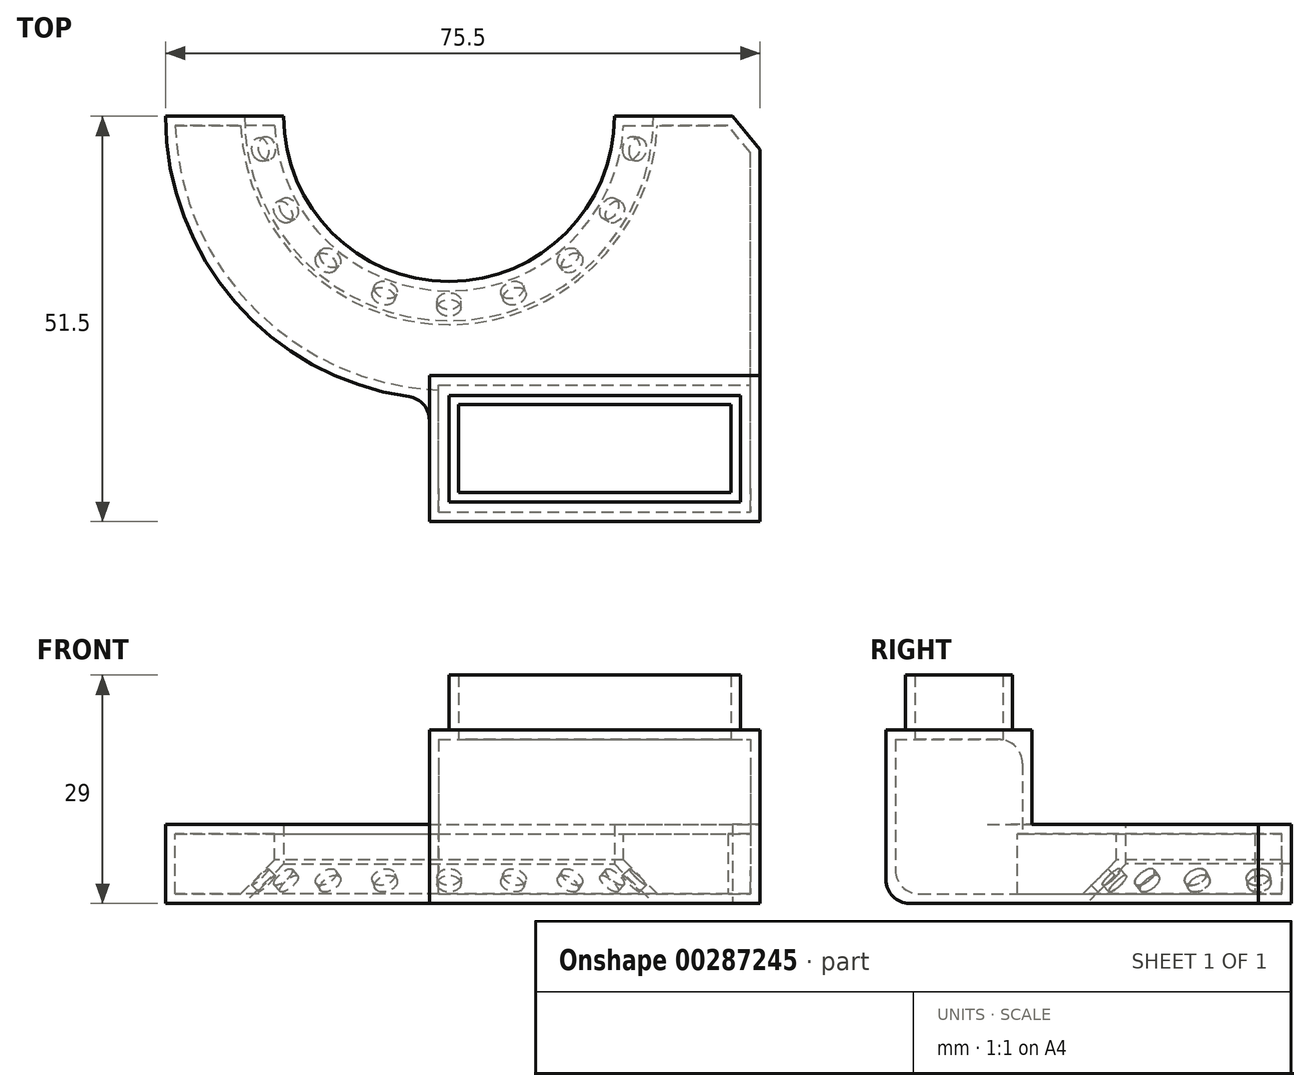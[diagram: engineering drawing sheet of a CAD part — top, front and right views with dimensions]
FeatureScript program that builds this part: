
annotation { "Feature Type Name" : "Feature", "Feature Type Description" : "" }
export const myFeature = defineFeature(function(context is Context, id is Id, definition is map)
    precondition{}
    {
        {
            var Q0;
            Q0=qCreatedBy(makeId("Front.planeOp"),FACE);
            var sketch = newSketch(context, id + "F0", { "sketchPlane" : qUnion([Q0])});
            skLineSegment(sketch, "E0", {"start": v(0, 66.2) * mm, "end": v(0, -56.66) * mm, "construction": true});
            skLineSegment(sketch, "E1", {"start": v(21, 10) * mm, "end": v(36, 10) * mm});
            skLineSegment(sketch, "E2", {"start": v(36, 10) * mm, "end": v(36, 0) * mm});
            skLineSegment(sketch, "E3", {"start": v(36, 0) * mm, "end": v(26, 0) * mm});
            skLineSegment(sketch, "E4", {"start": v(21, 10) * mm, "end": v(21, 5) * mm});
            skLineSegment(sketch, "E5", {"start": v(21, 5) * mm, "end": v(26, 0) * mm});
            skSolve(sketch);
        }
        {
            var Q0;
            Q0=makeQuery(id+"F0.imprint","IMPRINT",FACE,{"disambiguationData":[TD([[makeQuery(id+"F0.imprint","IMPRINT",EDGE,{"derivedFrom":sQuery(id+"F0.wireOp",EDGE,"E1")}),-1.0]])]});
            var Q1;
            Q1=sQuery(id+"F0.wireOp",EDGE,"E0");
            revolve(context, id + "F1", {"entities" : qUnion([Q0]), "axis" : qUnion([Q1]), "revolveType" : RevolveType.TWO_DIRECTIONS, "angle" : 180 * degree, "angleBack" : 360 * degree});
        }
        {
            var Q0;
            Q0=qCreatedBy(makeId("Top.planeOp"),FACE);
            var sketch = newSketch(context, id + "F2", { "sketchPlane" : qUnion([Q0])});
            skLineSegment(sketch, "E6.bottom", {"start": v(-2.5, -51.5) * mm, "end": v(39.5, -51.5) * mm});
            skLineSegment(sketch, "E6.left", {"start": v(-2.5, -51.5) * mm, "end": v(-2.5, -30.9) * mm});
            skLineSegment(sketch, "E6.right", {"start": v(39.5, -51.5) * mm, "end": v(39.5, -4.22) * mm});
            skPoint(sketch, "E7.orphan", {"position": v(26, 0) * mm});
            skPoint(sketch, "E8.orphan", {"position": v(-26, 0) * mm});
            skPoint(sketch, "E9.0", {"position": v(36, 0) * mm});
            skLineSegment(sketch, "E10", {"start": v(39.5, -4.22) * mm, "end": v(36, 0) * mm});
            skArc(sketch, "E11", {"start": v(-2.5, -30.9) * mm, "mid": v(21.02, -22.79) * mm, "end": v(31, 0) * mm});
            skLineSegment(sketch, "E12", {"start": v(36, 0) * mm, "end": v(31, 0) * mm});
            skSolve(sketch);
        }
        {
            var Q0;
            Q0=makeQuery(id+"F2.imprint","IMPRINT",FACE,{"disambiguationData":[TD([[makeQuery(id+"F2.imprint","IMPRINT",EDGE,{"derivedFrom":sQuery(id+"F2.wireOp",EDGE,"E6.bottom")}),1.0]])]});
            var Q1;
            Q1=makeQuery(id+"F1.opRevolve","SWEPT_FACE",FACE,{"disambiguationData":[OSD([sQuery(id+"F0.wireOp",EDGE,"E1")])]});
            extrude(context, id + "F3", {"entities" : qUnion([Q0]), "operationType" : NewBodyOperationType.ADD, "endBound" : BoundingType.UP_TO_SURFACE, "endBoundEntityFace" : qUnion([Q1]), "depth" : 25 * mm});
        }
        {
            var Q0;
            Q0=makeQuery(id+"F3.boolean.opBoolean","MERGE",FACE,{"derivedFrom":[makeQuery(id+"F1.opRevolve","SWEPT_FACE",FACE,{"disambiguationData":[OSD([sQuery(id+"F0.wireOp",EDGE,"E1")])]}),makeQuery(id+"F3.opExtrude","CAP_FACE",FACE,{"disambiguationData":[OSD([sQuery(id+"F2.wireOp",EDGE,"E6.bottom"),sQuery(id+"F2.wireOp",EDGE,"E6.left"),sQuery(id+"F2.wireOp",EDGE,"E6.right"),sQuery(id+"F2.wireOp",EDGE,"E10"),sQuery(id+"F2.wireOp",EDGE,"E11"),sQuery(id+"F2.wireOp",EDGE,"E12")])],"isStart":false})]});
            var sketch = newSketch(context, id + "F4", { "sketchPlane" : qUnion([Q0])});
            skPoint(sketch, "E13.0", {"position": v(-2.5, -51.5) * mm});
            skLineSegment(sketch, "E14.bottom", {"start": v(-2.5, -51.5) * mm, "end": v(39.5, -51.5) * mm});
            skLineSegment(sketch, "E14.top", {"start": v(-2.5, -32.96) * mm, "end": v(39.5, -32.96) * mm});
            skLineSegment(sketch, "E14.left", {"start": v(-2.5, -51.5) * mm, "end": v(-2.5, -32.96) * mm});
            skLineSegment(sketch, "E14.right", {"start": v(39.5, -51.5) * mm, "end": v(39.5, -32.96) * mm});
            skSolve(sketch);
        }
        {
            var Q0;
            Q0=makeQuery(id+"F4.imprint","IMPRINT",FACE,{"disambiguationData":[TD([[makeQuery(id+"F4.imprint","IMPRINT",EDGE,{"derivedFrom":sQuery(id+"F4.wireOp",EDGE,"E14.bottom")}),1.0]])]});
            extrude(context, id + "F5", {"entities" : qUnion([Q0]), "operationType" : NewBodyOperationType.ADD, "depth" : 12 * mm});
        }
        {
            var Q0;
            Q0=makeQuery(id+"F5.opExtrude","CAP_FACE",FACE,{"disambiguationData":[OSD([sQuery(id+"F4.wireOp",EDGE,"E14.bottom"),sQuery(id+"F4.wireOp",EDGE,"E14.top"),sQuery(id+"F4.wireOp",EDGE,"E14.left"),sQuery(id+"F4.wireOp",EDGE,"E14.right")])],"isStart":false});
            var sketch = newSketch(context, id + "F6", { "sketchPlane" : qUnion([Q0])});
            skPoint(sketch, "E15.0", {"position": v(-2.5, -32.96) * mm});
            skPoint(sketch, "E16.0", {"position": v(-2.5, -51.5) * mm});
            skPoint(sketch, "E17.0", {"position": v(39.5, -51.5) * mm});
            skPoint(sketch, "E18.0", {"position": v(39.5, -32.96) * mm});
            skLineSegment(sketch, "E19", {"start": v(-2.5, -32.96) * mm, "end": v(39.5, -51.5) * mm, "construction": true});
            skLineSegment(sketch, "E20", {"start": v(-2.5, -51.5) * mm, "end": v(39.5, -32.96) * mm, "construction": true});
            skLineSegment(sketch, "E21.bottom", {"start": v(37, -35.46) * mm, "end": v(0, -35.46) * mm});
            skLineSegment(sketch, "E21.top", {"start": v(37, -49) * mm, "end": v(0, -49) * mm});
            skLineSegment(sketch, "E21.left", {"start": v(37, -35.46) * mm, "end": v(37, -49) * mm});
            skLineSegment(sketch, "E21.right", {"start": v(0, -35.46) * mm, "end": v(0, -49) * mm});
            skPoint(sketch, "E21.middle", {"position": v(18.5, -42.23) * mm});
            skSolve(sketch);
        }
        {
            var Q0;
            Q0=makeQuery(id+"F6.imprint","IMPRINT",FACE,{"disambiguationData":[TD([[makeQuery(id+"F6.imprint","IMPRINT",EDGE,{"derivedFrom":sQuery(id+"F6.wireOp",EDGE,"E21.bottom")}),1.0]])]});
            extrude(context, id + "F7", {"entities" : qUnion([Q0]), "operationType" : NewBodyOperationType.ADD, "depth" : 7 * mm});
        }
        {
            var Q0;
            Q0=makeQuery(id+"F7.opExtrude","CAP_FACE",FACE,{"disambiguationData":[OSD([sQuery(id+"F6.wireOp",EDGE,"E21.bottom"),sQuery(id+"F6.wireOp",EDGE,"E21.top"),sQuery(id+"F6.wireOp",EDGE,"E21.left"),sQuery(id+"F6.wireOp",EDGE,"E21.right")])],"isStart":false});
            shell(context, id + "F8", {"entities" : qUnion([Q0]), "thickness" : 1.2 * mm});
        }
        {
            var Q0;
            Q0=qCreatedBy(makeId("Top.planeOp"),FACE);
            var sketch = newSketch(context, id + "F9", { "sketchPlane" : qUnion([Q0])});
            skLineSegment(sketch, "E22", {"start": v(71.7, 0) * mm, "end": v(-68.59, 0) * mm});
            skSolve(sketch);
        }
        {
            var Q0;
            Q0=sQuery(id+"F9.wireOp",EDGE,"E22");
            cPlane(context, id + "F10", {"entities" : qUnion([Q0]), "cplaneType" : CPlaneType.LINE_ANGLE, "offset" : 25 * mm, "angle" : 45 * degree, "width" : 150 * mm, "height" : 150 * mm});
        }
        {
            var Q0;
            Q0=qCreatedBy(id+"F10.planeOp",FACE);
            var sketch = newSketch(context, id + "F11", { "sketchPlane" : qUnion([Q0])});
            skCircle(sketch, "E23", {"center": v(0, -14.85) * mm, "radius": 1.5 * mm});
            skSolve(sketch);
        }
        {
            var Q0;
            Q0=makeQuery(id+"F11.imprint","IMPRINT",FACE,{"disambiguationData":[TD([[makeQuery(id+"F11.imprint","IMPRINT",EDGE,{"derivedFrom":sQuery(id+"F11.wireOp",EDGE,"E23")}),1.0]])]});
            extrude(context, id + "F12", {"entities" : qUnion([Q0]), "depth" : 25 * mm});
        }
        {
            var Q0;
            Q0=makeQuery(id+"F12.opExtrude","SWEPT_BODY",BODY,{"disambiguationData":[OSD([sQuery(id+"F11.wireOp",EDGE,"E23")])]});
            var Q1;
            Q1=sQuery(id+"F0.wireOp",EDGE,"E0");
            circularPattern(context, id + "F13", {"operationType" : NewBodyOperationType.REMOVE, "entities" : qUnion([Q0]), "axis" : qUnion([Q1]), "angle" : 360 * degree, "instanceCount" : 18, "equalSpace" : true});
        }
        {
            var Q0;
            Q0=makeQuery(id+"F3.opExtrude","CAP_EDGE",EDGE,{"disambiguationData":[OSD([sQuery(id+"F2.wireOp",EDGE,"E6.bottom")])],"isStart":true});
            var Q1;
            Q1=makeQuery(id+"F8.opShell","OFFSET_EDGE",EDGE,{"disambiguationData":[OSD([sQuery(id+"F2.wireOp",EDGE,"E6.bottom")])]});
            var Q2;
            {var subQ0=sQuery(id+"F4.wireOp",EDGE,"E14.top");Q2=makeQuery(id+"F8.opShell","OFFSET_EDGE",EDGE,{"disambiguationData":[OSD([subQ0]),TDD([makeQuery(id+"F5.opExtrude","CAP_EDGE",EDGE,{"disambiguationData":[OSD([subQ0])],"isStart":true})])]});}
            var Q3;
            Q3=makeQuery(id+"F5.opExtrude","CAP_EDGE",EDGE,{"disambiguationData":[OSD([sQuery(id+"F4.wireOp",EDGE,"E14.top")])],"isStart":true});
            var Q4;
            Q4=makeQuery(id+"F3.boolean.opBoolean","INTERSECT",EDGE,{"derivedFrom":[makeQuery(id+"F1.opRevolve","SWEPT_FACE",FACE,{"disambiguationData":[OSD([sQuery(id+"F0.wireOp",EDGE,"E2")])]}),makeQuery(id+"F3.opExtrude","SWEPT_FACE",FACE,{"disambiguationData":[OSD([sQuery(id+"F2.wireOp",EDGE,"E6.left")])]})]});
            var Q5;
            Q5=makeQuery(id+"F3.boolean.opBoolean","INTERSECT",EDGE,{"derivedFrom":[makeQuery(id+"F1.opRevolve","SWEPT_FACE",FACE,{"disambiguationData":[OSD([sQuery(id+"F0.wireOp",EDGE,"E2")])]}),makeQuery(id+"F3.opExtrude","SWEPT_FACE",FACE,{"disambiguationData":[OSD([sQuery(id+"F2.wireOp",EDGE,"E6.left")])]})]});
            fillet(context, id + "F14", {"entities" : qUnion([Q0, Q1, Q2, Q3, Q4, Q5]), "radius" : 3 * mm, "tangentPropagation" : true, "allowEdgeOverflow" : false});
        }
    });
